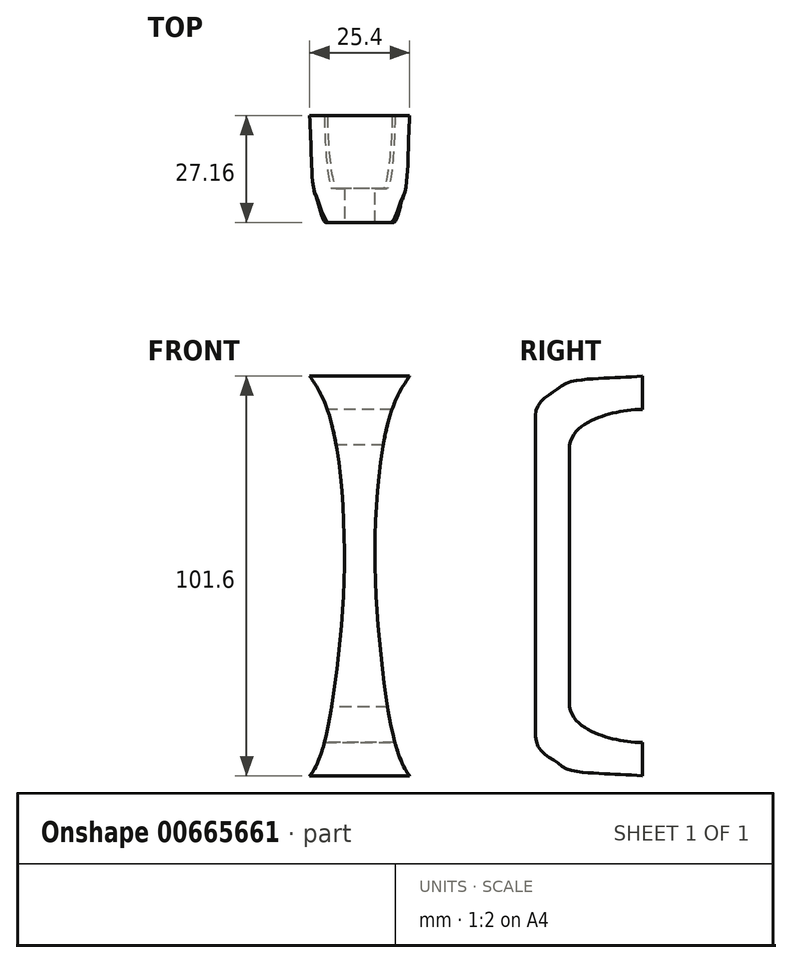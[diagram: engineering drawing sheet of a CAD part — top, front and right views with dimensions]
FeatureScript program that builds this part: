
annotation { "Feature Type Name" : "Feature", "Feature Type Description" : "" }
export const myFeature = defineFeature(function(context is Context, id is Id, definition is map)
    precondition{}
    {
        {
            var Q0;
            Q0=qCreatedBy(makeId("Front.planeOp"),FACE);
            var sketch = newSketch(context, id + "F0", { "sketchPlane" : qUnion([Q0])});
            skLineSegment(sketch, "E0.bottom", {"start": v(0, 0) * mm, "end": v(25.4, 0) * mm});
            skLineSegment(sketch, "E0.top", {"start": v(0, -101.6) * mm, "end": v(25.4, -101.6) * mm});
            skLineSegment(sketch, "E1", {"start": v(12.7, 0) * mm, "end": v(12.7, -101.6) * mm, "construction": true});
            skFitSpline(sketch, "E2", {"points": [v(0, 0) * mm, v(4.87, -9.65) * mm, v(8.78, -40.53) * mm, v(6.44, -78.17) * mm, v(0, -101.6) * mm], "startDerivative": vector(34.13, -49.44) * mm, "endDerivative": vector(-43.34, -54.63) * mm});
            skFitSpline(sketch, "E3.MirrorCS", {"points": [v(25.4, 0) * mm, v(20.53, -9.65) * mm, v(16.62, -40.53) * mm, v(18.96, -78.17) * mm, v(25.4, -101.6) * mm], "startDerivative": vector(-34.13, -49.44) * mm, "endDerivative": vector(43.34, -54.63) * mm});
            skSolve(sketch);
        }
        {
            var Q0;
            Q0=makeQuery(id+"F0.imprint","IMPRINT",FACE,{"disambiguationData":[TD([[makeQuery(id+"F0.imprint","IMPRINT",EDGE,{"derivedFrom":sQuery(id+"F0.wireOp",EDGE,"E0.bottom")}),-1.0]])]});
            extrude(context, id + "F1", {"entities" : qUnion([Q0]), "depth" : 38.86 * mm, "offsetDistance" : 25.4 * mm});
        }
        {
            var Q0;
            Q0=qCreatedBy(makeId("Right.planeOp"),FACE);
            var sketch = newSketch(context, id + "F2", { "sketchPlane" : qUnion([Q0])});
            skLineSegment(sketch, "E4", {"start": v(-18.52, 8.53) * mm, "end": v(-18.52, -113.34) * mm, "construction": true});
            skLineSegment(sketch, "E5", {"start": v(-27.16, 10.6) * mm, "end": v(-27.16, -114.23) * mm, "construction": true});
            skFitSpline(sketch, "E6", {"points": [v(0, 0) * mm, v(-18.52, -1.5) * mm, v(-21.79, -3.48) * mm, v(-27.16, -10.08) * mm], "startDerivative": vector(-38.4, -3.34) * mm, "endDerivative": vector(0, -35.72) * mm});
            skLineSegment(sketch, "E7", {"start": v(-50.31, -50.8) * mm, "end": v(57.1, -50.8) * mm, "construction": true});
            skLineSegment(sketch, "E8", {"start": v(-34.08, -50.8) * mm, "end": v(-34.08, 0) * mm, "construction": true});
            skLineSegment(sketch, "E9", {"start": v(-34.08, -50.8) * mm, "end": v(-34.08, -101.6) * mm, "construction": true});
            skFitSpline(sketch, "E10", {"points": [v(-18.52, -17.51) * mm, v(-11.86, -10.84) * mm, v(0, -8.55) * mm], "startDerivative": vector(4.6, 22.6) * mm, "endDerivative": vector(22.22, -0.66) * mm});
            skFitSpline(sketch, "E11.MirrorCS", {"points": [v(-18.52, -84.09) * mm, v(-11.86, -90.76) * mm, v(0, -93.05) * mm], "startDerivative": vector(4.6, -22.6) * mm, "endDerivative": vector(22.22, 0.66) * mm});
            skFitSpline(sketch, "E12.MirrorCS", {"points": [v(0, -101.6) * mm, v(-18.52, -100.1) * mm, v(-21.79, -98.12) * mm, v(-27.16, -91.52) * mm], "startDerivative": vector(-38.4, 3.34) * mm, "endDerivative": vector(0, 35.72) * mm});
            skLineSegment(sketch, "E13", {"start": v(-27.16, -91.52) * mm, "end": v(-27.16, -10.08) * mm});
            skLineSegment(sketch, "E14", {"start": v(-18.52, -17.51) * mm, "end": v(-18.52, -84.09) * mm});
            skLineSegment(sketch, "E15", {"start": v(0, 0) * mm, "end": v(0, -8.55) * mm});
            skLineSegment(sketch, "E16", {"start": v(0, -93.05) * mm, "end": v(0, -101.6) * mm});
            skSolve(sketch);
        }
        {
            var Q0;
            Q0 = qSketchRegion(id + "F2", true);
            extrude(context, id + "F3", {"entities" : qUnion([Q0]), "operationType" : NewBodyOperationType.INTERSECT, "depth" : 73.66 * mm, "offsetDistance" : 25.4 * mm});
        }
    });
